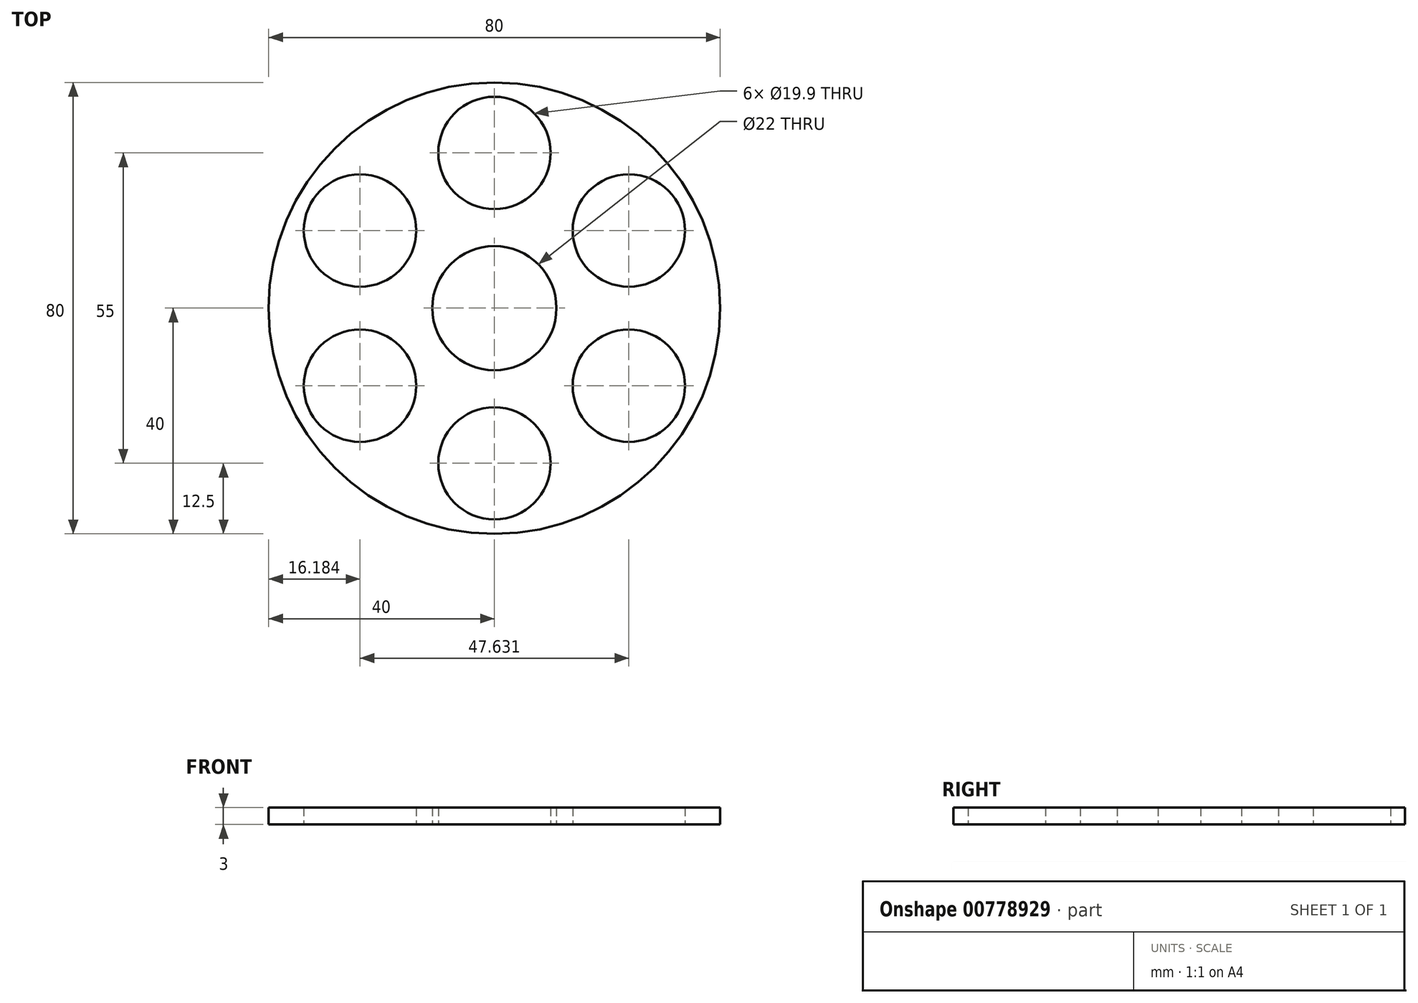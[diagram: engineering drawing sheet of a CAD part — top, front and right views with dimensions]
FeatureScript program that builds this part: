
annotation { "Feature Type Name" : "Feature", "Feature Type Description" : "" }
export const myFeature = defineFeature(function(context is Context, id is Id, definition is map)
    precondition{}
    {
        {
            var Q0;
            Q0=qCreatedBy(makeId("Top.planeOp"),FACE);
            var sketch = newSketch(context, id + "F0", { "sketchPlane" : qUnion([Q0])});
            skCircle(sketch, "E0", {"center": v(0, 0) * mm, "radius": 11 * mm});
            skCircle(sketch, "E1", {"center": v(0, 0) * mm, "radius": 40 * mm});
            skCircle(sketch, "E2", {"center": v(0, 27.5) * mm, "radius": 9.95 * mm});
            skCircle(sketch, "E3", {"center": v(-23.82, 13.75) * mm, "radius": 9.95 * mm});
            skCircle(sketch, "E4", {"center": v(23.82, 13.75) * mm, "radius": 9.95 * mm});
            skLineSegment(sketch, "E5.trimOffspring", {"start": v(-32.43, 18.73) * mm, "end": v(-30.16, 21.41) * mm});
            skCircle(sketch, "E6.1.1", {"center": v(-23.82, -13.75) * mm, "radius": 9.95 * mm});
            skCircle(sketch, "E6.1.2", {"center": v(0, -27.5) * mm, "radius": 9.95 * mm});
            skCircle(sketch, "E6.2.0", {"center": v(0, -27.5) * mm, "radius": 9.95 * mm});
            skCircle(sketch, "E6.2.1", {"center": v(23.82, -13.75) * mm, "radius": 9.95 * mm});
            skSolve(sketch);
        }
        {
            var Q0;
            Q0 = qSketchRegion(id + "F0", true);
            extrude(context, id + "F1", {"entities" : qUnion([Q0]), "depth" : 3 * mm, "offsetDistance" : 25 * mm});
        }
    });
